# Revit family: Rollenlager Duo,  M10 bis dreiviertel Zoll
name_source: partatom
category: HLS-Bauteile
revit_build: Autodesk Revit 2017 (Build: 20190507_1515(x64)
units: mm (PartAtom-declared; Revit-internal decimal feet)

## family parameters
Basisbauteil = Fläche
Beim Laden mit Abzugskörper schneiden = Nein
Bemaßung runder Anschluss = Durchmesser verwenden
Gemeinsam genutzt = Ja
Raumberechnungspunkt = Nein
Teiletyp = Normal

## types (5) — shared parameters
Breite = 120 mm  [stored 0.393701 ft]
Fabrikat = MEFA
Firma = MEFA Befestigungs- und Montagesysteme GmbH
Kurztext1 = Rollenlager Duo axial
Lochabstand = 100 mm
Länge = 380 mm
Material = Stahl
Materialname = S235
Mengeneinheit = St
Oberflaeche = galvanisch verzinkt
Rollwiderstand = 0,004 - 0,02
Vorgabe-Ansicht = 1219 mm
max. Schiebeweg axial = 120 mm
max. Temperaturbeständigkeit = 300 °C
max. zul. Last Druck = 8000.00 N
max. zul. Last Zug = 8000.00 N
vpe = 1 St

## per-type parameters (varying)
| type | Anschluss | Artikelnummer | Bauhöhe | EAN | Gewicht | Gewicht pro Bauteil | Kurztext2 | Typ |
| Rollenlager Duo M10 | 2xM10 | 175911811 | 65 mm | 4250928448811 | 4.05 kg | 4.05 kg | Anschluss 2xM10 | Rollenlager duo, axial 2xM10 |
| Rollenlager Duo M12 | 2xM12 | 175911813 | 65 mm | 4250928448828 | 4.02 kg | 4.02 kg | Anschluss 2xM12 | Rollenlager duo, axial 2xM12 |
| Rollenlager Duo M16 | 2xM16 | 175911816 | 65 mm | 4250928448835 | 4.13 kg | 4.13 kg | Anschluss 2xM16 | Rollenlager duo, axial 2xM16 |
| Rollenlager Duo 1/2" | 2x1/2'' | 175911839 | 45 mm | 4250928448842 | 4.03 kg | 4.03 kg | Anschluss 2x1/2'' | Rollenlager duo, axial 2xHalbzoll |
| Rollenlager Duo 3/4" | 2x3/4'' | 175911840 | 86 mm | 4250928448859 | 4.38 kg | 4.38 kg | Anschluss 2x3/4'' | Rollenlager duo, axial 2xdreiviertelzoll |

note: [stored X ft] marks values corroborated as IEEE doubles in the binary element streams (Revit-internal decimal feet)
